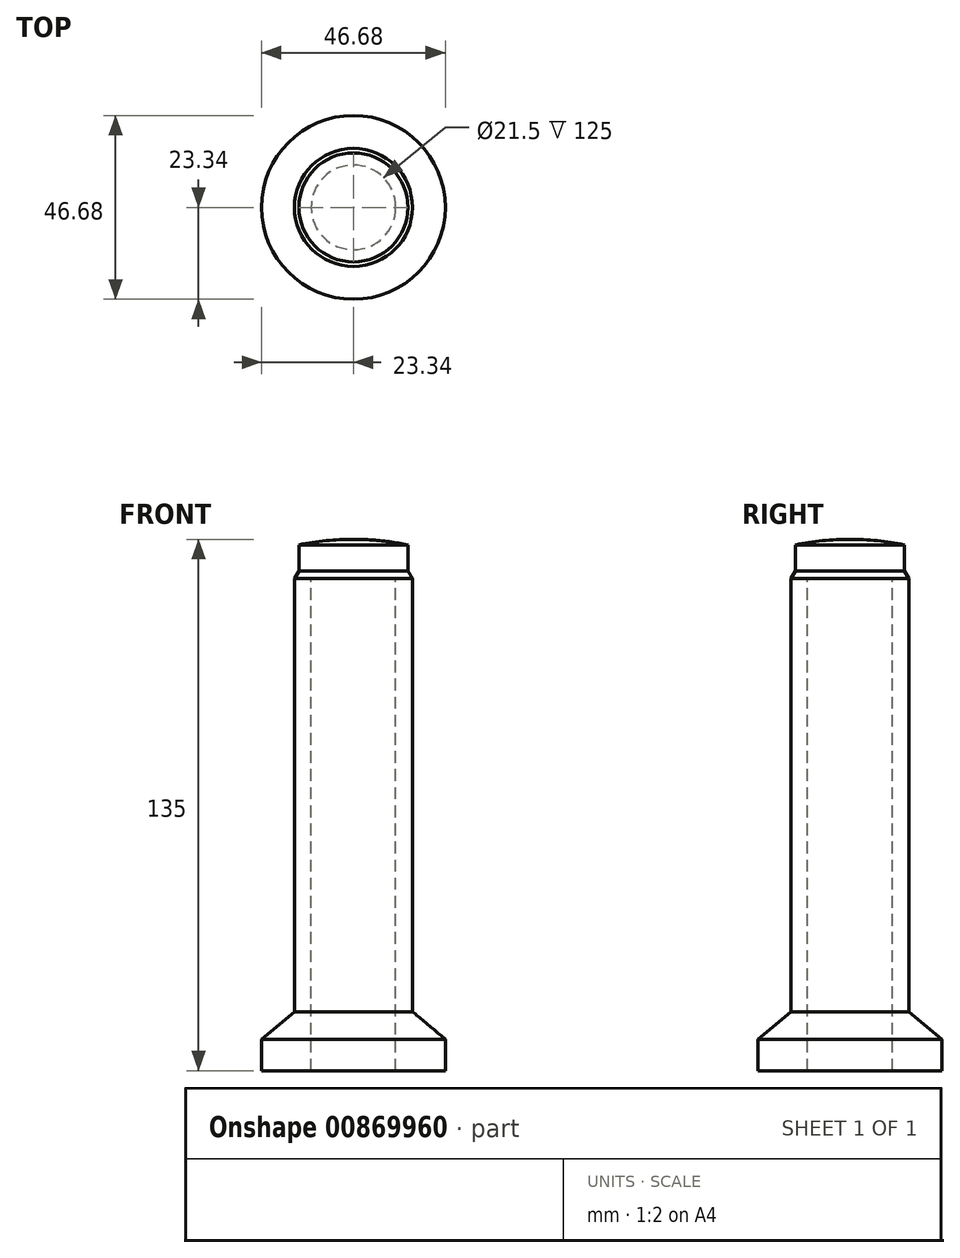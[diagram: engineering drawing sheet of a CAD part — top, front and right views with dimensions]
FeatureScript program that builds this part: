
annotation { "Feature Type Name" : "Feature", "Feature Type Description" : "" }
export const myFeature = defineFeature(function(context is Context, id is Id, definition is map)
    precondition{}
    {
        {
            var Q0;
            Q0=qCreatedBy(makeId("Front.planeOp"),FACE);
            var sketch = newSketch(context, id + "F0", { "sketchPlane" : qUnion([Q0])});
            skLineSegment(sketch, "E0", {"start": v(0, 17.76) * mm, "end": v(0, 0) * mm, "construction": true});
            skLineSegment(sketch, "E1", {"start": v(0, 135) * mm, "end": v(0, 125) * mm});
            skLineSegment(sketch, "E2", {"start": v(0, 125) * mm, "end": v(10.75, 125) * mm});
            skLineSegment(sketch, "E3", {"start": v(10.75, 125) * mm, "end": v(10.75, 0) * mm});
            skLineSegment(sketch, "E4", {"start": v(10.75, 0) * mm, "end": v(23.34, 0) * mm});
            skLineSegment(sketch, "E5", {"start": v(23.34, 0) * mm, "end": v(23.34, 8) * mm});
            skLineSegment(sketch, "E6", {"start": v(23.34, 8) * mm, "end": v(15, 15) * mm});
            skLineSegment(sketch, "E7", {"start": v(15, 15) * mm, "end": v(15, 125) * mm});
            skPoint(sketch, "E7.endSnap0", {"position": v(5.37, 125) * mm});
            skLineSegment(sketch, "E8", {"start": v(15, 125) * mm, "end": v(13.85, 127) * mm});
            skLineSegment(sketch, "E9", {"start": v(13.85, 127) * mm, "end": v(13.85, 133.58) * mm});
            skArc(sketch, "E10", {"start": v(13.85, 133.58) * mm, "mid": v(6.96, 134.64) * mm, "end": v(0, 135) * mm});
            skSolve(sketch);
        }
        {
            var Q0;
            Q0=makeQuery(id+"F0.imprint","IMPRINT",FACE,{"disambiguationData":[TD([[makeQuery(id+"F0.imprint","IMPRINT",EDGE,{"derivedFrom":sQuery(id+"F0.wireOp",EDGE,"E1")}),1.0]])]});
            var Q1;
            Q1=sQuery(id+"F0.wireOp",EDGE,"E0");
            revolve(context, id + "F1", {"surfaceOperationType" : NewSurfaceOperationType.NEW, "entities" : qUnion([Q0]), "axis" : qUnion([Q1]), "revolveType" : RevolveType.FULL});
        }
    });
